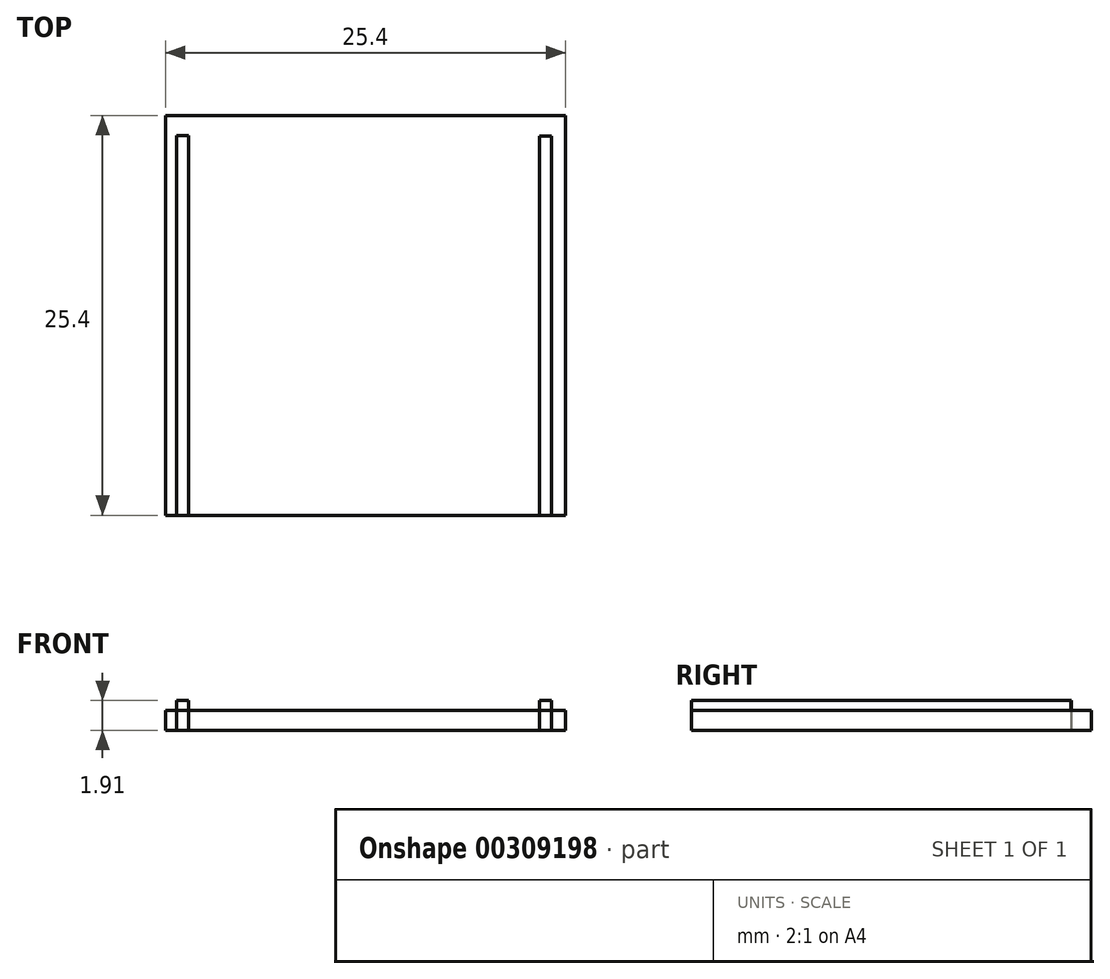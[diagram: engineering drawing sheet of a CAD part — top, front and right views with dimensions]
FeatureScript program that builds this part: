
annotation { "Feature Type Name" : "Feature", "Feature Type Description" : "" }
export const myFeature = defineFeature(function(context is Context, id is Id, definition is map)
    precondition{}
    {
        {
            var Q0;
            Q0=qCreatedBy(makeId("Top.planeOp"),FACE);
            var sketch = newSketch(context, id + "F0", { "sketchPlane" : qUnion([Q0])});
            skLineSegment(sketch, "E0.bottom", {"start": v(12.75, -14.54) * mm, "end": v(-12.65, -14.54) * mm});
            skLineSegment(sketch, "E0.top", {"start": v(12.75, 10.86) * mm, "end": v(-12.65, 10.86) * mm});
            skLineSegment(sketch, "E0.left", {"start": v(12.75, -14.54) * mm, "end": v(12.75, 10.86) * mm});
            skLineSegment(sketch, "E0.right", {"start": v(-12.65, -14.54) * mm, "end": v(-12.65, 10.86) * mm});
            skPoint(sketch, "E0.middle", {"position": v(0.05, -1.84) * mm});
            skLineSegment(sketch, "E1", {"start": v(-11.94, 9.59) * mm, "end": v(-11.94, -14.54) * mm});
            skLineSegment(sketch, "E2", {"start": v(-11.18, 9.59) * mm, "end": v(-11.18, -14.54) * mm});
            skLineSegment(sketch, "E3", {"start": v(-11.94, 9.59) * mm, "end": v(-11.18, 9.59) * mm});
            skLineSegment(sketch, "E4", {"start": v(11.08, 9.56) * mm, "end": v(11.08, -14.54) * mm});
            skLineSegment(sketch, "E5", {"start": v(11.85, 9.56) * mm, "end": v(11.85, -14.54) * mm});
            skLineSegment(sketch, "E6", {"start": v(11.08, 9.56) * mm, "end": v(11.85, 9.56) * mm});
            skSolve(sketch);
        }
        {
            var Q0;
            {var subQ0=sQuery(id+"F0.wireOp",EDGE,"E4");Q0=makeQuery(id+"F0.imprint","IMPRINT",FACE,{"disambiguationData":[TD([[makeQuery(id+"F0.imprint","IMPRINT",EDGE,{"derivedFrom":subQ0}),1.0]])]});}
            var Q1;
            {var subQ0=sQuery(id+"F0.wireOp",EDGE,"E1");Q1=makeQuery(id+"F0.imprint","IMPRINT",FACE,{"disambiguationData":[TD([[makeQuery(id+"F0.imprint","IMPRINT",EDGE,{"derivedFrom":subQ0}),1.0]])]});}
            extrude(context, id + "F1", {"entities" : qUnion([Q0, Q1]), "depth" : 1.9 * mm});
        }
        {
            var Q0;
            Q0=makeQuery(id+"F0.imprint","IMPRINT",FACE,{"disambiguationData":[TD([[makeQuery(id+"F0.imprint","IMPRINT",EDGE,{"derivedFrom":sQuery(id+"F0.wireOp",EDGE,"E0.top")}),1.0]])]});
            var Q1;
            {var subQ0=sQuery(id+"F0.wireOp",EDGE,"E1");Q1=makeQuery(id+"F0.imprint","IMPRINT",FACE,{"disambiguationData":[TD([[makeQuery(id+"F0.imprint","IMPRINT",EDGE,{"derivedFrom":subQ0}),1.0]])]});}
            var Q2;
            {var subQ0=sQuery(id+"F0.wireOp",EDGE,"E4");Q2=makeQuery(id+"F0.imprint","IMPRINT",FACE,{"disambiguationData":[TD([[makeQuery(id+"F0.imprint","IMPRINT",EDGE,{"derivedFrom":subQ0}),1.0]])]});}
            extrude(context, id + "F2", {"entities" : qUnion([Q0, Q1, Q2]), "depth" : 1.27 * mm});
        }
    });
